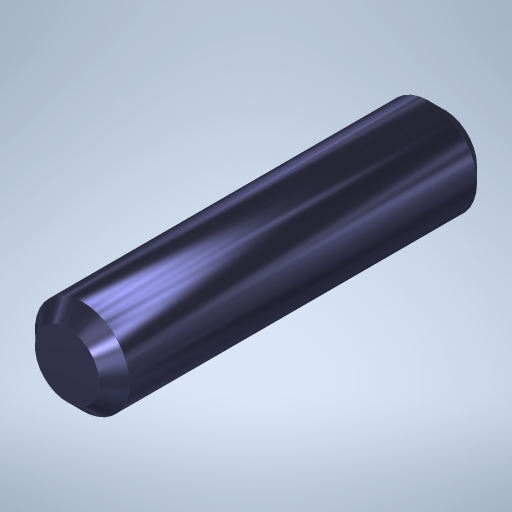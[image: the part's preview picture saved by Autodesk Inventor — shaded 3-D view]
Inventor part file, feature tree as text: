
AUTODESK INVENTOR PART (.ipt)
format: ipt  version: 2023.1 (Build 271208000, 208)  size: 277,504 bytes
history: native  units: in
note: dims shown in document units (in); Inventor stores cm internally (conversion verified against a paired STEP export)
features: extrude x1, chamfer x1, sketch x1
ambient origin geometry x8: Origin, YZ Plane, XZ Plane, XY Plane, X Axis, Y Axis, Z Axis, Center Point
bodies: Solid1 (feature_tree)
feature tree (3):
  extrude  "Extrusion1"  Depth=0.375in TaperAngle=0.0deg
  chamfer  "Chamfer1"  Distance=0.015in Angle=45.0deg
  sketch  "Sketch1"  dims[d0=0.0938in d1=0.375in d2=0.0in d3=0.015in d4=0.125in d5=45.0deg]
